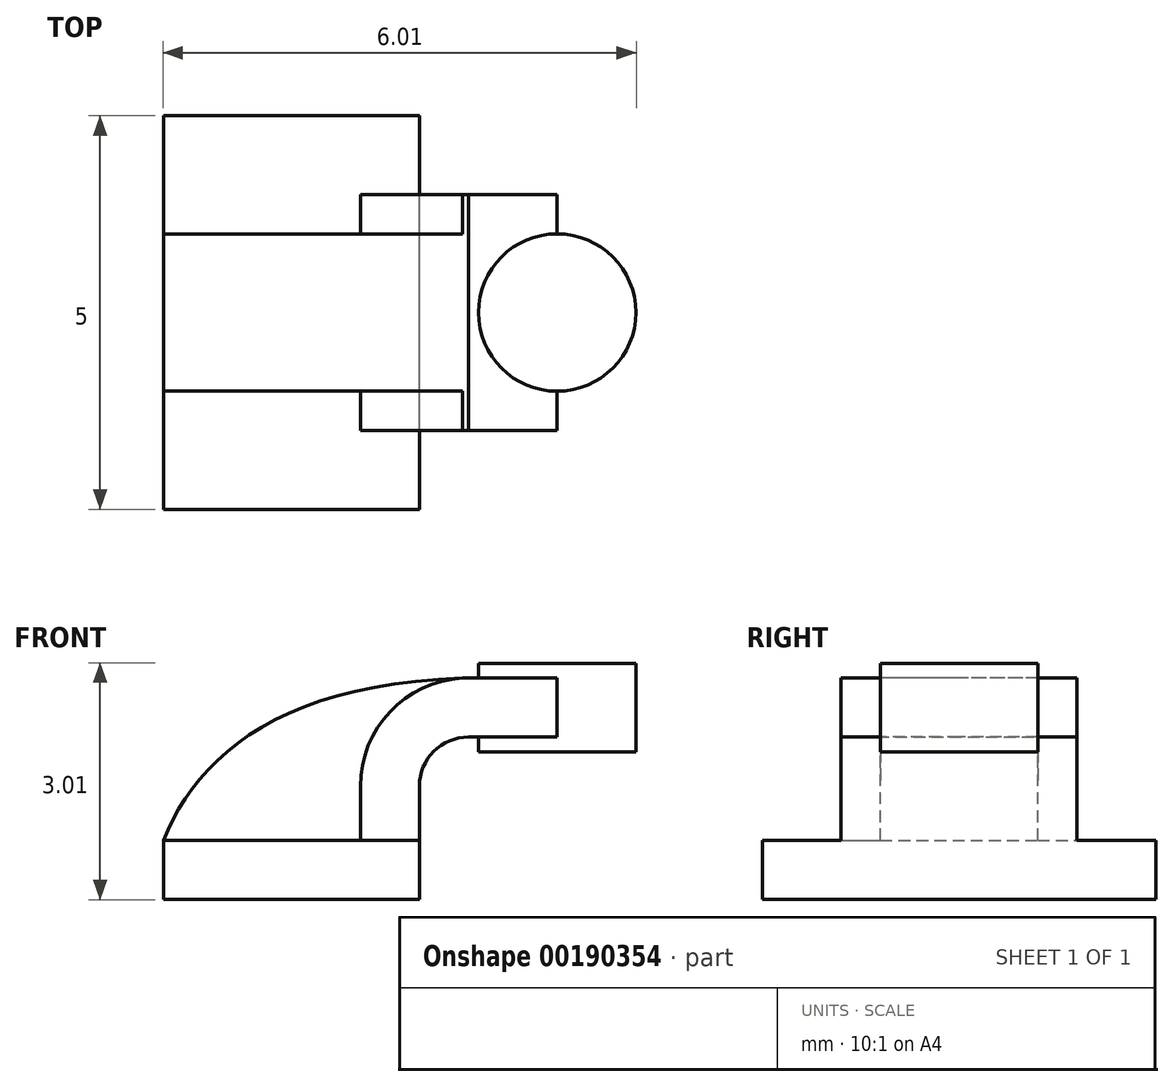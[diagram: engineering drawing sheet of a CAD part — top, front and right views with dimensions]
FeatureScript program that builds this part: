
annotation { "Feature Type Name" : "Feature", "Feature Type Description" : "" }
export const myFeature = defineFeature(function(context is Context, id is Id, definition is map)
    precondition{}
    {
        {
            var Q0;
            Q0=qCreatedBy(makeId("Front.planeOp"),FACE);
            var sketch = newSketch(context, id + "F0", { "sketchPlane" : qUnion([Q0])});
            skLineSegment(sketch, "E0.bottom", {"start": v(1.62, 0.38) * mm, "end": v(-1.62, 0.38) * mm});
            skLineSegment(sketch, "E0.top", {"start": v(1.63, -0.37) * mm, "end": v(-1.62, -0.37) * mm});
            skLineSegment(sketch, "E0.left", {"start": v(1.63, 0.38) * mm, "end": v(1.63, -0.37) * mm});
            skLineSegment(sketch, "E0.right", {"start": v(-1.62, 0.38) * mm, "end": v(-1.62, -0.37) * mm});
            skPoint(sketch, "E0.middle", {"position": v(0, 0) * mm});
            skLineSegment(sketch, "E1.bottom", {"start": v(4.38, 1.5) * mm, "end": v(2.37, 1.5) * mm});
            skLineSegment(sketch, "E1.top", {"start": v(4.37, 2.63) * mm, "end": v(2.38, 2.63) * mm});
            skLineSegment(sketch, "E1.left", {"start": v(4.37, 1.5) * mm, "end": v(4.37, 2.63) * mm});
            skLineSegment(sketch, "E1.right", {"start": v(2.37, 1.5) * mm, "end": v(2.38, 2.63) * mm});
            skPoint(sketch, "E1.middle", {"position": v(3.37, 2.06) * mm});
            skLineSegment(sketch, "E2", {"start": v(1.62, 0.38) * mm, "end": v(1.62, 1.06) * mm});
            skArc(sketch, "E3", {"start": v(1.62, 1.06) * mm, "mid": v(1.8, 1.5) * mm, "end": v(2.25, 1.69) * mm});
            skLineSegment(sketch, "E4", {"start": v(2.25, 1.69) * mm, "end": v(3.37, 1.69) * mm});
            skLineSegment(sketch, "E5.0", {"start": v(2.25, 2.44) * mm, "end": v(3.37, 2.44) * mm});
            skArc(sketch, "E5.1", {"start": v(0.87, 1.06) * mm, "mid": v(1.28, 2.04) * mm, "end": v(2.25, 2.44) * mm});
            skLineSegment(sketch, "E5.2", {"start": v(0.88, 0.38) * mm, "end": v(0.88, 1.06) * mm});
            skLineSegment(sketch, "E6", {"start": v(3.37, 1.5) * mm, "end": v(3.37, 2.63) * mm});
            skFitSpline(sketch, "E7", {"points": [v(-1.62, 0.38) * mm, v(2.25, 2.44) * mm], "startDerivative": vector(1.25, 3.12) * mm, "endDerivative": vector(7.29, 0.18) * mm});
            skSolve(sketch);
        }
        {
            var Q0;
            Q0=makeQuery(id+"F0.imprint","IMPRINT",FACE,{"disambiguationData":[TD([[makeQuery(id+"F0.imprint","IMPRINT",EDGE,{"derivedFrom":sQuery(id+"F0.wireOp",EDGE,"E0.top")}),-1.0]])]});
            extrude(context, id + "F1", {"entities" : qUnion([Q0]), "endBound" : BoundingType.SYMMETRIC, "depth" : 5 * mm});
        }
        {
            var Q0;
            {var subQ1=sQuery(id+"F0.wireOp",EDGE,"E2");Q0=makeQuery(id+"F0.imprint","IMPRINT",FACE,{"disambiguationData":[TD([[makeQuery(id+"F0.imprint","IMPRINT",EDGE,{"derivedFrom":subQ1}),1.0]])]});}
            var Q1;
            {var subQ0=sQuery(id+"F0.wireOp",EDGE,"E4");var subQ1=sQuery(id+"F0.wireOp",EDGE,"E1.right");var subQ2=makeQuery(id+"F0.imprint","INTERSECT",VERTEX,{"derivedFrom":[subQ1,subQ0]});Q1=makeQuery(id+"F0.imprint","IMPRINT",FACE,{"disambiguationData":[TD([[makeQuery(id+"F0.imprint","IMPRINT",EDGE,{"disambiguationData":[TD([[subQ2,-1.0]])],"derivedFrom":subQ1}),-1.0]])]});}
            extrude(context, id + "F2", {"entities" : qUnion([Q0, Q1]), "operationType" : NewBodyOperationType.ADD, "endBound" : BoundingType.SYMMETRIC, "depth" : 3 * mm});
        }
        {
            var Q0;
            {var subQ3=sQuery(id+"F0.wireOp",EDGE,"E5.2");Q0=makeQuery(id+"F0.imprint","IMPRINT",FACE,{"disambiguationData":[TD([[makeQuery(id+"F0.imprint","IMPRINT",EDGE,{"derivedFrom":subQ3}),1.0]])]});}
            extrude(context, id + "F3", {"entities" : qUnion([Q0]), "operationType" : NewBodyOperationType.ADD, "endBound" : BoundingType.SYMMETRIC, "depth" : 2 * mm});
        }
        {
            var Q0;
            {var subQ0=sQuery(id+"F0.wireOp",EDGE,"E1.left");Q0=makeQuery(id+"F0.imprint","IMPRINT",FACE,{"disambiguationData":[TD([[makeQuery(id+"F0.imprint","IMPRINT",EDGE,{"derivedFrom":subQ0}),1.0]])]});}
            var Q1;
            Q1=sQuery(id+"F0.wireOp",EDGE,"E6");
            revolve(context, id + "F4", {"operationType" : NewBodyOperationType.ADD, "entities" : qUnion([Q0]), "axis" : qUnion([Q1]), "revolveType" : RevolveType.FULL});
        }
    });
